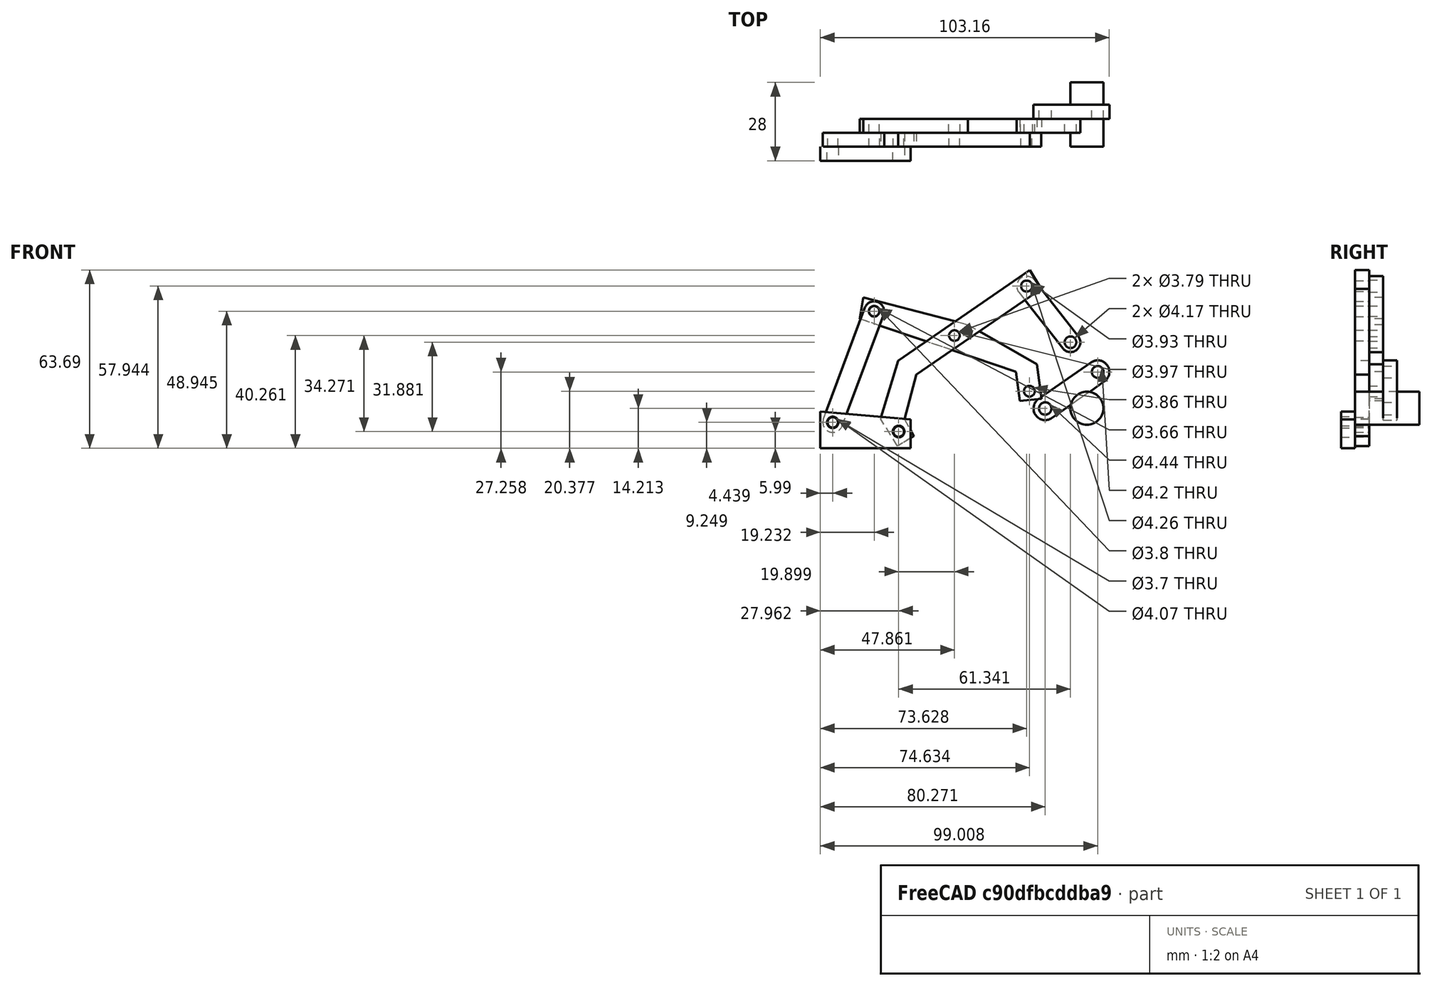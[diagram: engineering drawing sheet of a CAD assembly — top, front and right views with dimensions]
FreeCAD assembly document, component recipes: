
FREECAD ASSEMBLY — COMPONENT RECIPES ("TestMeca1-1")

This assembly document has 7 components, labeled P0..P6 below (a component is one placed body or linked part). 7 of them carry a construction recipe — the FreeCAD feature program that regenerates the part from scratch, quoted from this document or its linked companion documents; the rest are supplied as boundary geometry only. No exploded tour is included for this assembly.
COMPONENT P0 — recipe-attached ("Corps", modeled in this document).
Construction recipe (the document's own serialized feature program — sketch geometry with constraints, then the solid features built on it; lengths are millimeters unless a unit is written):

FEATURE [Sketcher::SketchObject] Sketch
  ArcFitTolerance = 1e-06
  AttachmentSupport = -> [Origin002]
  ExternalTypes = [0]
  FullyConstrained = false
  MakeInternals = false
  MapMode = 5
  Placement = pos=(0,0,0) rot=(1,0,0;1.5708rad)
  sketch-geometry (6):
    g0: LineSegment StartX=0 StartY=0 StartZ=0 EndX=0 EndY=13.138 EndZ=0
    g1: LineSegment StartX=0 StartY=13.138 StartZ=0 EndX=32.2081 EndY=10.2743 EndZ=0
    g2: LineSegment StartX=32.2081 StartY=10.2743 StartZ=0 EndX=32.2081 EndY=0 EndZ=0
    g3: LineSegment StartX=32.2081 StartY=0 StartZ=0 EndX=0 EndY=0 EndZ=0
    g4: Circle CenterX=27.9622 CenterY=5.98985 CenterZ=0 NormalX=0 NormalY=0 NormalZ=1 AngleXU=0 Radius=2.08292
    g5: Circle CenterX=4.43862 CenterY=9.24882 CenterZ=0 NormalX=0 NormalY=0 NormalZ=1 AngleXU=0 Radius=2.03403
  constraints (8):
    c: Coincident(g-1,g0)
    c: PointOnObject(g0,g-2)
    c: Coincident(g0,g1)
    c: Coincident(g1,g2)
    c: PointOnObject(g2,g-1)
    c: Vertical(g2)
    c: Coincident(g2,g3)
    c: Coincident(g3,g0)
FEATURE [PartDesign::Pad] Pad
  Direction = (0,-1,0)
  Length = 5
  Length2 = 10
  Profile = -> Sketch
  ReferenceAxis = -> Sketch [N_Axis]
  Refine = true
  SideType = 0
  Suppressed = false
  Type = 0
  Type2 = 0
FEATURE [PartDesign::Body] Body  label="Corps"
  AllowCompound = false
  Group = -> [Sketch,Pad]
  Origin = -> Origin002
  Tip = -> Pad
COMPONENT P1 — recipe-attached ("Corps001", modeled in this document).
Construction recipe (the document's own serialized feature program — sketch geometry with constraints, then the solid features built on it; lengths are millimeters unless a unit is written):

FEATURE [Sketcher::SketchObject] Sketch001
  ArcFitTolerance = 1e-06
  AttachmentSupport = -> [Origin004]
  ExternalTypes = [0]
  FullyConstrained = false
  MakeInternals = false
  MapMode = 5
  Placement = pos=(0,0,0) rot=(1,0,0;1.5708rad)
  sketch-geometry (6):
    g0: ArcOfCircle CenterX=4.3933 CenterY=9.28745 CenterZ=0 NormalX=0 NormalY=0 NormalZ=1 AngleXU=0 Radius=3.55115 StartAngle=3.65377 EndAngle=6.79537
    g1: ArcOfCircle CenterX=-16.3679 CenterY=46.2142 CenterZ=0 NormalX=0 NormalY=0 NormalZ=1 AngleXU=0 Radius=3.55115 StartAngle=0.512182 EndAngle=3.65377
    g2: LineSegment StartX=1.29784 StartY=7.5471 StartZ=0 EndX=-19.4634 EndY=44.4739 EndZ=0
    g3: LineSegment StartX=7.48876 StartY=11.0278 StartZ=0 EndX=-13.2724 EndY=47.9545 EndZ=0
    g4: Circle CenterX=-16.3679 CenterY=46.2142 CenterZ=0 NormalX=0 NormalY=0 NormalZ=1 AngleXU=0 Radius=1.89824
    g5: Circle CenterX=4.3933 CenterY=9.28745 CenterZ=0 NormalX=0 NormalY=0 NormalZ=1 AngleXU=0 Radius=1.85066
  constraints (7):
    c: Tangent(g0,g2) = 1.5708
    c: Tangent(g0,g3) = -1.5708
    c: Tangent(g1,g2) = 1.5708
    c: Tangent(g1,g3) = -1.5708
    c: Equal(g0,g1)
    c: Coincident(g4,g1)
    c: Coincident(g5,g0)
FEATURE [PartDesign::Pad] Pad001
  Direction = (0,-1,2e-16)
  Length = 5
  Length2 = 10
  Profile = -> Sketch001
  ReferenceAxis = -> Sketch001 [N_Axis]
  Refine = true
  SideType = 0
  Suppressed = false
  Type = 0
  Type2 = 0
FEATURE [PartDesign::Body] Body001  label="Corps001"
  AllowCompound = false
  Group = -> [Sketch001,Pad001]
  Origin = -> Origin004
  Placement = pos=(-5.49004,5,6.60695) rot=(0,1,0;0.868892rad)
  Tip = -> Pad001
COMPONENT P2 — recipe-attached ("Corps002", modeled in this document).
Construction recipe (the document's own serialized feature program — sketch geometry with constraints, then the solid features built on it; lengths are millimeters unless a unit is written):

FEATURE [Sketcher::SketchObject] Sketch002
  ArcFitTolerance = 1e-06
  AttachmentSupport = -> [Origin006]
  ExternalTypes = [0]
  FullyConstrained = false
  MakeInternals = false
  MapMode = 5
  Placement = pos=(0,0,0) rot=(1,0,0;1.5708rad)
  sketch-geometry (6):
    g0: ArcOfCircle CenterX=9.93968 CenterY=74.2901 CenterZ=0 NormalX=0 NormalY=0 NormalZ=1 AngleXU=0 Radius=3.51304 StartAngle=0.499119 EndAngle=3.64071
    g1: ArcOfCircle CenterX=22.1303 CenterY=51.9285 CenterZ=0 NormalX=0 NormalY=0 NormalZ=1 AngleXU=0 Radius=3.51304 StartAngle=3.64071 EndAngle=6.7823
    g2: LineSegment StartX=13.0241 StartY=75.9716 StartZ=0 EndX=25.2148 EndY=53.61 EndZ=0
    g3: LineSegment StartX=6.85522 StartY=72.6086 StartZ=0 EndX=19.0458 EndY=50.247 EndZ=0
    g4: Circle CenterX=9.93968 CenterY=74.2901 CenterZ=0 NormalX=0 NormalY=0 NormalZ=1 AngleXU=0 Radius=2.12816
    g5: Circle CenterX=22.1303 CenterY=51.9285 CenterZ=0 NormalX=0 NormalY=0 NormalZ=1 AngleXU=0 Radius=2.08513
  constraints (7):
    c: Tangent(g0,g2) = 1.5708
    c: Tangent(g0,g3) = -1.5708
    c: Tangent(g1,g2) = 1.5708
    c: Tangent(g1,g3) = -1.5708
    c: Equal(g0,g1)
    c: Coincident(g4,g0)
    c: Coincident(g5,g1)
FEATURE [PartDesign::Pad] Pad002
  Direction = (0,-1,2e-16)
  Length = 5
  Length2 = 10
  Profile = -> Sketch002
  ReferenceAxis = -> Sketch002 [N_Axis]
  Refine = true
  SideType = 0
  Suppressed = false
  Type = 0
  Type2 = 0
FEATURE [PartDesign::Body] Body002  label="Corps002"
  AllowCompound = false
  Group = -> [Sketch002,Pad002]
  Origin = -> Origin006
  Placement = pos=(75.9415,10,-16.972) rot=(0,-1,0;0.16388rad)
  Tip = -> Pad002
COMPONENT P3 — recipe-attached ("Corps004", modeled in this document).
Construction recipe (the document's own serialized feature program — sketch geometry with constraints, then the solid features built on it; lengths are millimeters unless a unit is written):

FEATURE [Sketcher::SketchObject] Sketch004
  ArcFitTolerance = 1e-06
  AttachmentSupport = -> [Origin010]
  ExternalTypes = [0]
  FullyConstrained = false
  MakeInternals = false
  MapMode = 5
  Placement = pos=(0,0,0) rot=(1,0,0;1.5708rad)
  sketch-geometry (10):
    g0: LineSegment StartX=-23.6072 StartY=51.3966 StartZ=0 EndX=-21.2757 EndY=58.8351 EndZ=0
    g1: LineSegment StartX=-21.2757 StartY=58.8351 StartZ=0 EndX=14.4735 EndY=44.1801 EndZ=0
    g2: LineSegment StartX=14.4735 StartY=44.1801 StartZ=0 EndX=37.011 EndY=26.9717 EndZ=0
    g3: LineSegment StartX=37.011 StartY=26.9717 StartZ=0 EndX=37.011 EndY=14.5372 EndZ=0
    g4: LineSegment StartX=37.011 StartY=14.5372 StartZ=0 EndX=29.2394 EndY=14.8702 EndZ=0
    g5: LineSegment StartX=29.2394 StartY=14.8702 StartZ=0 EndX=29.2394 EndY=25.3063 EndZ=0
    g6: LineSegment StartX=29.2394 StartY=25.3063 StartZ=0 EndX=-23.6072 EndY=51.3966 EndZ=0
    g7: Circle CenterX=33.061 CenterY=17.7892 CenterZ=0 NormalX=0 NormalY=0 NormalZ=1 AngleXU=0 Radius=1.92887
    g8: Circle CenterX=9.13695 CenterY=41.0232 CenterZ=0 NormalX=0 NormalY=0 NormalZ=1 AngleXU=0 Radius=1.9865
    g9: Circle CenterX=-18.1003 CenterY=53.3997 CenterZ=0 NormalX=0 NormalY=0 NormalZ=1 AngleXU=0 Radius=1.8317
  constraints (9):
    c: Coincident(g0,g1)
    c: Coincident(g1,g2)
    c: Coincident(g2,g3)
    c: Vertical(g3)
    c: Coincident(g3,g4)
    c: Coincident(g4,g5)
    c: Vertical(g5)
    c: Coincident(g5,g6)
    c: Coincident(g6,g0)
FEATURE [PartDesign::Pad] Pad004
  Direction = (0,-1,0)
  Length = 5
  Length2 = 10
  Profile = -> Sketch004
  ReferenceAxis = -> Sketch004 [N_Axis]
  Refine = true
  SideType = 0
  Suppressed = false
  Type = 0
  Type2 = 0
FEATURE [PartDesign::Body] Body004  label="Corps004"
  AllowCompound = false
  Group = -> [Sketch004,Pad004]
  Origin = -> Origin010
  Placement = pos=(44.202,10,-1.60818) rot=(0,-1,0;0.131988rad)
  Tip = -> Pad004
COMPONENT P4 — recipe-attached ("Corps005", modeled in this document).
Construction recipe (the document's own serialized feature program — sketch geometry with constraints, then the solid features built on it; lengths are millimeters unless a unit is written):

FEATURE [Sketcher::SketchObject] Sketch005
  ArcFitTolerance = 1e-06
  AttachmentSupport = -> [Origin012]
  ExternalTypes = [0]
  FullyConstrained = false
  MakeInternals = false
  MapMode = 5
  Placement = pos=(0,0,0) rot=(1,0,0;1.5708rad)
  sketch-geometry (11):
    g0: LineSegment StartX=3.31041 StartY=76.0954 StartZ=0 EndX=11.193 EndY=76.0954 EndZ=0
    g1: LineSegment StartX=11.193 StartY=76.0954 StartZ=0 EndX=13.8575 EndY=22.0275 EndZ=0
    g2: LineSegment StartX=13.8575 StartY=22.0275 StartZ=0 EndX=25.3278 EndY=10.0553 EndZ=0
    g3: LineSegment StartX=25.3278 StartY=10.0553 StartZ=0 EndX=32.1894 EndY=9.81025 EndZ=0
    g4: LineSegment StartX=32.1894 StartY=9.81025 StartZ=0 EndX=32.1894 EndY=2.90781 EndZ=0
    g5: LineSegment StartX=32.1894 StartY=2.90781 StartZ=0 EndX=20.7126 EndY=2.90781 EndZ=0
    g6: LineSegment StartX=20.7126 StartY=2.90781 StartZ=0 EndX=6.25418 EndY=19.1224 EndZ=0
    g7: LineSegment StartX=6.25418 StartY=19.1224 StartZ=0 EndX=3.31041 EndY=76.0954 EndZ=0
    g8: Circle CenterX=7.62181 CenterY=72.1475 CenterZ=0 NormalX=0 NormalY=0 NormalZ=1 AngleXU=0 Radius=1.96538
    g9: Circle CenterX=9.17842 CenterY=40.9348 CenterZ=0 NormalX=0 NormalY=0 NormalZ=1 AngleXU=0 Radius=1.89735
    g10: Circle CenterX=27.9374 CenterY=6.02718 CenterZ=0 NormalX=0 NormalY=0 NormalZ=1 AngleXU=0 Radius=1.89735
  constraints (11):
    c: Horizontal(g0)
    c: Coincident(g0,g1)
    c: Coincident(g1,g2)
    c: Coincident(g2,g3)
    c: Coincident(g3,g4)
    c: Vertical(g4)
    c: Coincident(g4,g5)
    c: Horizontal(g5)
    c: Coincident(g5,g6)
    c: Coincident(g6,g7)
    c: Coincident(g7,g0)
FEATURE [PartDesign::Pad] Pad005
  Direction = (0,-1,0)
  Length = 5
  Length2 = 10
  Profile = -> Sketch005
  ReferenceAxis = -> Sketch005 [N_Axis]
  Refine = true
  SideType = 0
  Suppressed = false
  Type = 0
  Type2 = 0
FEATURE [PartDesign::Body] Body005  label="Corps005"
  AllowCompound = false
  Group = -> [Sketch005,Pad005]
  Origin = -> Origin012
  Placement = pos=(8.18757,5,26.6245) rot=(0,1,0;1.01916rad)
  Tip = -> Pad005
COMPONENT P5 — recipe-attached ("Corps003", modeled in this document).
Construction recipe (the document's own serialized feature program — sketch geometry with constraints, then the solid features built on it; lengths are millimeters unless a unit is written):

FEATURE [Sketcher::SketchObject] Sketch003
  ArcFitTolerance = 1e-06
  AttachmentSupport = -> [Origin008]
  ExternalTypes = [0]
  FullyConstrained = false
  MakeInternals = false
  MapMode = 5
  Placement = pos=(0,0,0) rot=(1,0,0;1.5708rad)
  sketch-geometry (6):
    g0: ArcOfCircle CenterX=33.0045 CenterY=40.5366 CenterZ=0 NormalX=0 NormalY=0 NormalZ=1 AngleXU=0 Radius=4.15593 StartAngle=1e-16 EndAngle=3.14159
    g1: ArcOfCircle CenterX=33.0045 CenterY=17.7064 CenterZ=0 NormalX=0 NormalY=0 NormalZ=1 AngleXU=0 Radius=4.15593 StartAngle=3.14159 EndAngle=6.28319
    g2: LineSegment StartX=37.1605 StartY=40.5366 StartZ=0 EndX=37.1605 EndY=17.7064 EndZ=0
    g3: LineSegment StartX=28.8486 StartY=40.5366 StartZ=0 EndX=28.8486 EndY=17.7064 EndZ=0
    g4: Circle CenterX=33.0045 CenterY=40.5366 CenterZ=0 NormalX=0 NormalY=0 NormalZ=1 AngleXU=0 Radius=2.09794
    g5: Circle CenterX=33.0045 CenterY=17.7064 CenterZ=0 NormalX=0 NormalY=0 NormalZ=1 AngleXU=0 Radius=2.22145
  constraints (8):
    c: Tangent(g0,g2) = 1.5708
    c: Tangent(g0,g3) = -1.5708
    c: Tangent(g1,g2) = 1.5708
    c: Tangent(g1,g3) = -1.5708
    c: Equal(g0,g1)
    c: Vertical(g2)
    c: Coincident(g4,g0)
    c: Coincident(g5,g1)
FEATURE [PartDesign::Pad] Pad003
  Direction = (0,-1,0)
  Length = 5
  Length2 = 10
  Profile = -> Sketch003
  ReferenceAxis = -> Sketch003 [N_Axis]
  Refine = true
  SideType = 0
  Suppressed = false
  Type = 0
  Type2 = 0
FEATURE [PartDesign::Body] Body003  label="Corps003"
  AllowCompound = false
  Group = -> [Sketch003,Pad003]
  Origin = -> Origin008
  Placement = pos=(46.8816,15,31.1819) rot=(0,1,0;0.962596rad)
  Tip = -> Pad003
COMPONENT P6 — recipe-attached ("Corps006", modeled in this document).
Construction recipe (the document's own serialized feature program — sketch geometry with constraints, then the solid features built on it; lengths are millimeters unless a unit is written):

FEATURE [Sketcher::SketchObject] Sketch006
  ArcFitTolerance = 1e-06
  AttachmentSupport = -> [Origin016]
  ExternalTypes = [0]
  FullyConstrained = false
  MakeInternals = false
  MapMode = 5
  Placement = pos=(0,0,0) rot=(1,0,0;1.5708rad)
  sketch-geometry (1):
    g0: Circle CenterX=95.172 CenterY=14.315 CenterZ=0 NormalX=0 NormalY=0 NormalZ=1 AngleXU=0 Radius=5.91026
FEATURE [PartDesign::Pad] Pad006
  Direction = (0,-1,2e-16)
  Length = 23
  Length2 = 10
  Profile = -> Sketch006
  ReferenceAxis = -> Sketch006 [N_Axis]
  Refine = true
  Reversed = true
  SideType = 0
  Suppressed = false
  Type = 0
  Type2 = 0
FEATURE [PartDesign::Body] Body006  label="Corps006"
  AllowCompound = false
  Group = -> [Sketch006,Pad006]
  Origin = -> Origin016
  Tip = -> Pad006
PROVENANCE & LICENSES
A FreeCAD (.FCStd) document from a public repository crawl; recipes are the document's own serialized feature recipes (and, for linked parts, companion documents' recipes).
License: as declared in the source repository (recorded in the dataset sidecar).
